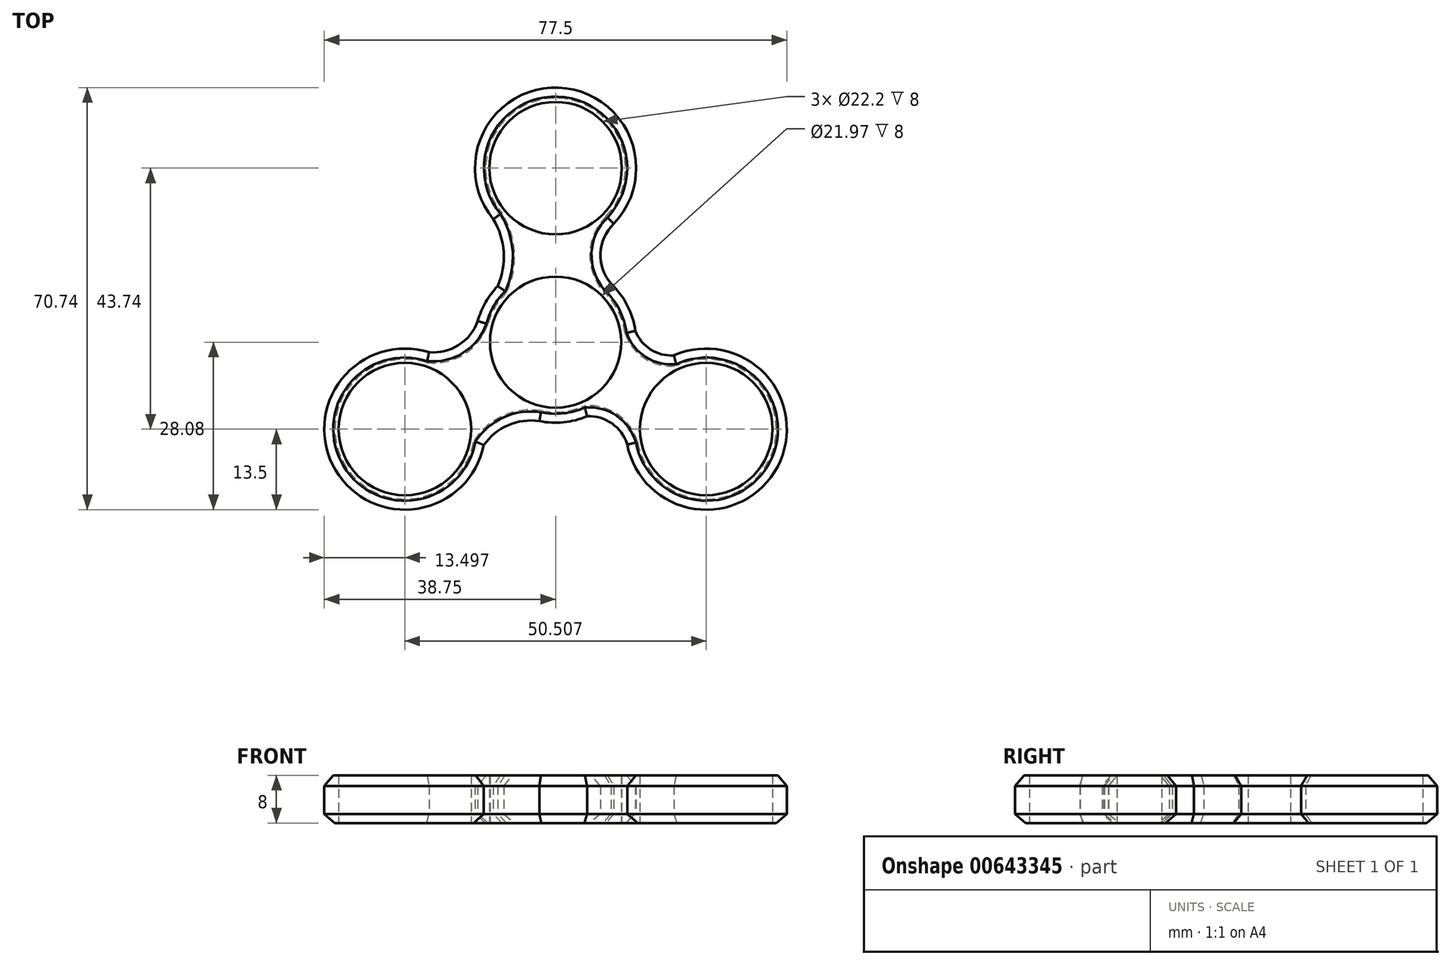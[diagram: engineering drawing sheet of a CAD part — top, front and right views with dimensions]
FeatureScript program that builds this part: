
annotation { "Feature Type Name" : "Feature", "Feature Type Description" : "" }
export const myFeature = defineFeature(function(context is Context, id is Id, definition is map)
    precondition{}
    {
        {
            var Q0;
            Q0=qCreatedBy(makeId("Top.planeOp"),FACE);
            var sketch = newSketch(context, id + "F0", { "sketchPlane" : qUnion([Q0])});
            skCircle(sketch, "E0", {"center": v(0, 0) * mm, "radius": 10.99 * mm});
            skCircle(sketch, "E1", {"center": v(0, 0) * mm, "radius": 13.5 * mm});
            skCircle(sketch, "E2", {"center": v(0, 29.16) * mm, "radius": 11.1 * mm});
            skCircle(sketch, "E3", {"center": v(0, 29.16) * mm, "radius": 13.5 * mm});
            skCircle(sketch, "E4.1.0", {"center": v(-25.25, -14.58) * mm, "radius": 11.1 * mm});
            skCircle(sketch, "E4.2.0", {"center": v(25.25, -14.58) * mm, "radius": 11.1 * mm});
            skCircle(sketch, "E5.1.0", {"center": v(-25.25, -14.58) * mm, "radius": 13.5 * mm});
            skCircle(sketch, "E5.2.0", {"center": v(25.25, -14.58) * mm, "radius": 13.5 * mm});
            skArc(sketch, "E6", {"start": v(-9.69, 9.4) * mm, "mid": v(-8.68, 15.1) * mm, "end": v(-10.44, 20.6) * mm});
            skArc(sketch, "E7", {"start": v(9.76, 19.84) * mm, "mid": v(7.53, 14.92) * mm, "end": v(9.27, 9.81) * mm});
            skArc(sketch, "E8", {"start": v(-21.2, -1.7) * mm, "mid": v(-16.22, -0.47) * mm, "end": v(-13.03, 3.55) * mm});
            skArc(sketch, "E9", {"start": v(-2.71, -13.22) * mm, "mid": v(-7.94, -13.91) * mm, "end": v(-12.02, -17.25) * mm});
            skArc(sketch, "E10", {"start": v(12, -17.17) * mm, "mid": v(9.46, -13.64) * mm, "end": v(5.28, -12.43) * mm});
            skArc(sketch, "E11", {"start": v(13.36, 1.91) * mm, "mid": v(15.92, -1.22) * mm, "end": v(19.84, -2.21) * mm});
            skSolve(sketch);
        }
        {
            var Q0;
            Q0=makeQuery(id+"F0.imprint","IMPRINT",FACE,{"disambiguationData":[TD([[makeQuery(id+"F0.imprint","IMPRINT",EDGE,{"derivedFrom":sQuery(id+"F0.wireOp",EDGE,"E2")}),-1.0]])]});
            var Q1;
            Q1=makeQuery(id+"F0.imprint","IMPRINT",FACE,{"disambiguationData":[TD([[makeQuery(id+"F0.imprint","IMPRINT",EDGE,{"derivedFrom":sQuery(id+"F0.wireOp",EDGE,"E0")}),-1.0]])]});
            var Q2;
            Q2=makeQuery(id+"F0.imprint","IMPRINT",FACE,{"disambiguationData":[TD([[makeQuery(id+"F0.imprint","IMPRINT",EDGE,{"derivedFrom":sQuery(id+"F0.wireOp",EDGE,"E4.1.0")}),-1.0]])]});
            var Q3;
            Q3=makeQuery(id+"F0.imprint","IMPRINT",FACE,{"disambiguationData":[TD([[makeQuery(id+"F0.imprint","IMPRINT",EDGE,{"derivedFrom":sQuery(id+"F0.wireOp",EDGE,"E4.2.0")}),-1.0]])]});
            var Q4;
            {var subQ0=sQuery(id+"F0.wireOp",EDGE,"E10");Q4=makeQuery(id+"F0.imprint","IMPRINT",FACE,{"disambiguationData":[TD([[makeQuery(id+"F0.imprint","IMPRINT",EDGE,{"derivedFrom":subQ0}),-1.0]])]});}
            var Q5;
            {var subQ0=sQuery(id+"F0.wireOp",EDGE,"E8");Q5=makeQuery(id+"F0.imprint","IMPRINT",FACE,{"disambiguationData":[TD([[makeQuery(id+"F0.imprint","IMPRINT",EDGE,{"derivedFrom":subQ0}),-1.0]])]});}
            var Q6;
            {var subQ0=sQuery(id+"F0.wireOp",EDGE,"E6");Q6=makeQuery(id+"F0.imprint","IMPRINT",FACE,{"disambiguationData":[TD([[makeQuery(id+"F0.imprint","IMPRINT",EDGE,{"derivedFrom":subQ0}),-1.0]])]});}
            extrude(context, id + "F1", {"entities" : qUnion([Q0, Q1, Q2, Q3, Q4, Q5, Q6]), "depth" : 8 * mm});
        }
        {
            var Q0;
            Q0=makeQuery(id+"F1.opExtrude","CAP_EDGE",EDGE,{"disambiguationData":[OSD([sQuery(id+"F0.wireOp",EDGE,"E5.1.0")])],"isStart":false});
            var Q1;
            Q1=makeQuery(id+"F1.opExtrude","CAP_EDGE",EDGE,{"disambiguationData":[OSD([sQuery(id+"F0.wireOp",EDGE,"E9")])],"isStart":false});
            var Q2;
            Q2=makeQuery(id+"F1.opExtrude","CAP_EDGE",EDGE,{"disambiguationData":[OSD([sQuery(id+"F0.wireOp",EDGE,"E8")])],"isStart":false});
            var Q3;
            {var subQ0=sQuery(id+"F0.wireOp",EDGE,"E1");Q3=makeQuery(id+"F1.opExtrude","CAP_EDGE",EDGE,{"disambiguationData":[OSD([subQ0]),TDD([makeQuery(id+"F0.imprint","IMPRINT",EDGE,{"disambiguationData":[TD([[makeQuery(id+"F0.imprint","INTERSECT",VERTEX,{"derivedFrom":[subQ0,sQuery(id+"F0.wireOp",EDGE,"E6")]}),-1.0]])],"derivedFrom":subQ0})])],"isStart":false});}
            var Q4;
            Q4=makeQuery(id+"F1.opExtrude","CAP_EDGE",EDGE,{"disambiguationData":[OSD([sQuery(id+"F0.wireOp",EDGE,"E6")])],"isStart":false});
            var Q5;
            Q5=makeQuery(id+"F1.opExtrude","CAP_EDGE",EDGE,{"disambiguationData":[OSD([sQuery(id+"F0.wireOp",EDGE,"E3")])],"isStart":false});
            var Q6;
            Q6=makeQuery(id+"F1.opExtrude","CAP_EDGE",EDGE,{"disambiguationData":[OSD([sQuery(id+"F0.wireOp",EDGE,"E7")])],"isStart":false});
            var Q7;
            {var subQ0=sQuery(id+"F0.wireOp",EDGE,"E1");Q7=makeQuery(id+"F1.opExtrude","CAP_EDGE",EDGE,{"disambiguationData":[OSD([subQ0]),TDD([makeQuery(id+"F0.imprint","IMPRINT",EDGE,{"disambiguationData":[TD([[makeQuery(id+"F0.imprint","INTERSECT",VERTEX,{"derivedFrom":[subQ0,sQuery(id+"F0.wireOp",EDGE,"E7")]}),1.0]])],"derivedFrom":subQ0})])],"isStart":false});}
            var Q8;
            Q8=makeQuery(id+"F1.opExtrude","CAP_EDGE",EDGE,{"disambiguationData":[OSD([sQuery(id+"F0.wireOp",EDGE,"E11")])],"isStart":false});
            var Q9;
            Q9=makeQuery(id+"F1.opExtrude","CAP_EDGE",EDGE,{"disambiguationData":[OSD([sQuery(id+"F0.wireOp",EDGE,"E5.2.0")])],"isStart":false});
            var Q10;
            Q10=makeQuery(id+"F1.opExtrude","CAP_EDGE",EDGE,{"disambiguationData":[OSD([sQuery(id+"F0.wireOp",EDGE,"E10")])],"isStart":false});
            var Q11;
            {var subQ0=sQuery(id+"F0.wireOp",EDGE,"E1");Q11=makeQuery(id+"F1.opExtrude","CAP_EDGE",EDGE,{"disambiguationData":[OSD([subQ0]),TDD([makeQuery(id+"F0.imprint","IMPRINT",EDGE,{"disambiguationData":[TD([[makeQuery(id+"F0.imprint","INTERSECT",VERTEX,{"derivedFrom":[subQ0,sQuery(id+"F0.wireOp",EDGE,"E9")]}),-1.0]])],"derivedFrom":subQ0})])],"isStart":false});}
            chamfer(context, id + "F2", {"entities" : qUnion([Q0, Q1, Q2, Q3, Q4, Q5, Q6, Q7, Q8, Q9, Q10, Q11]), "chamferType" : ChamferType.OFFSET_ANGLE, "width" : 1.5 * mm, "oppositeDirection" : false, "angle" : 50 * degree, "tangentPropagation" : true});
        }
        {
            var Q0;
            Q0=makeQuery(id+"F1.opExtrude","CAP_EDGE",EDGE,{"disambiguationData":[OSD([sQuery(id+"F0.wireOp",EDGE,"E3")])],"isStart":true});
            var Q1;
            Q1=makeQuery(id+"F1.opExtrude","CAP_EDGE",EDGE,{"disambiguationData":[OSD([sQuery(id+"F0.wireOp",EDGE,"E6")])],"isStart":true});
            var Q2;
            Q2=makeQuery(id+"F1.opExtrude","CAP_EDGE",EDGE,{"disambiguationData":[OSD([sQuery(id+"F0.wireOp",EDGE,"E7")])],"isStart":true});
            var Q3;
            {var subQ0=sQuery(id+"F0.wireOp",EDGE,"E1");Q3=makeQuery(id+"F1.opExtrude","CAP_EDGE",EDGE,{"disambiguationData":[OSD([subQ0]),TDD([makeQuery(id+"F0.imprint","IMPRINT",EDGE,{"disambiguationData":[TD([[makeQuery(id+"F0.imprint","INTERSECT",VERTEX,{"derivedFrom":[subQ0,sQuery(id+"F0.wireOp",EDGE,"E7")]}),1.0]])],"derivedFrom":subQ0})])],"isStart":true});}
            var Q4;
            Q4=makeQuery(id+"F1.opExtrude","CAP_EDGE",EDGE,{"disambiguationData":[OSD([sQuery(id+"F0.wireOp",EDGE,"E11")])],"isStart":true});
            var Q5;
            Q5=makeQuery(id+"F1.opExtrude","CAP_EDGE",EDGE,{"disambiguationData":[OSD([sQuery(id+"F0.wireOp",EDGE,"E5.2.0")])],"isStart":true});
            var Q6;
            Q6=makeQuery(id+"F1.opExtrude","CAP_EDGE",EDGE,{"disambiguationData":[OSD([sQuery(id+"F0.wireOp",EDGE,"E10")])],"isStart":true});
            var Q7;
            {var subQ0=sQuery(id+"F0.wireOp",EDGE,"E1");Q7=makeQuery(id+"F1.opExtrude","CAP_EDGE",EDGE,{"disambiguationData":[OSD([subQ0]),TDD([makeQuery(id+"F0.imprint","IMPRINT",EDGE,{"disambiguationData":[TD([[makeQuery(id+"F0.imprint","INTERSECT",VERTEX,{"derivedFrom":[subQ0,sQuery(id+"F0.wireOp",EDGE,"E9")]}),-1.0]])],"derivedFrom":subQ0})])],"isStart":true});}
            var Q8;
            {var subQ0=sQuery(id+"F0.wireOp",EDGE,"E1");Q8=makeQuery(id+"F1.opExtrude","CAP_EDGE",EDGE,{"disambiguationData":[OSD([subQ0]),TDD([makeQuery(id+"F0.imprint","IMPRINT",EDGE,{"disambiguationData":[TD([[makeQuery(id+"F0.imprint","INTERSECT",VERTEX,{"derivedFrom":[subQ0,sQuery(id+"F0.wireOp",EDGE,"E6")]}),-1.0]])],"derivedFrom":subQ0})])],"isStart":true});}
            var Q9;
            Q9=makeQuery(id+"F1.opExtrude","CAP_EDGE",EDGE,{"disambiguationData":[OSD([sQuery(id+"F0.wireOp",EDGE,"E8")])],"isStart":true});
            var Q10;
            Q10=makeQuery(id+"F1.opExtrude","CAP_EDGE",EDGE,{"disambiguationData":[OSD([sQuery(id+"F0.wireOp",EDGE,"E5.1.0")])],"isStart":true});
            var Q11;
            Q11=makeQuery(id+"F1.opExtrude","CAP_EDGE",EDGE,{"disambiguationData":[OSD([sQuery(id+"F0.wireOp",EDGE,"E9")])],"isStart":true});
            chamfer(context, id + "F3", {"entities" : qUnion([Q0, Q1, Q2, Q3, Q4, Q5, Q6, Q7, Q8, Q9, Q10, Q11]), "chamferType" : ChamferType.OFFSET_ANGLE, "width" : 1.5 * mm, "oppositeDirection" : false, "angle" : 50 * degree, "tangentPropagation" : true});
        }
    });
